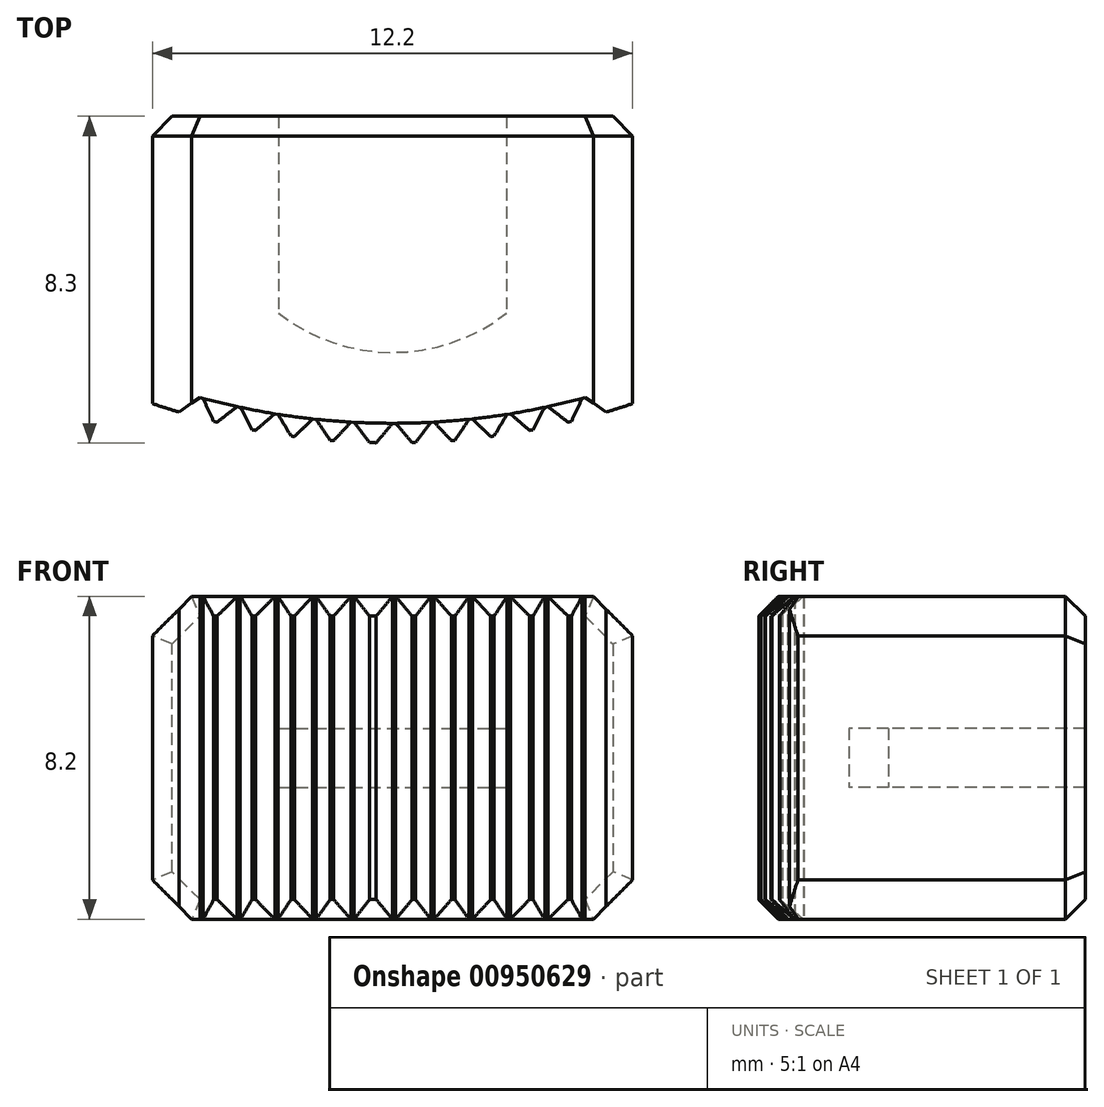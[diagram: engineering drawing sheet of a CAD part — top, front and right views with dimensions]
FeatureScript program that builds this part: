
annotation { "Feature Type Name" : "Feature", "Feature Type Description" : "" }
export const myFeature = defineFeature(function(context is Context, id is Id, definition is map)
    precondition{}
    {
        {
            var Q0;
            Q0=qCreatedBy(makeId("Top.planeOp"),FACE);
            var sketch = newSketch(context, id + "F0", { "sketchPlane" : qUnion([Q0])});
            skLineSegment(sketch, "E0", {"start": v(-6.1, -3.15) * mm, "end": v(-6.1, 4.15) * mm});
            skLineSegment(sketch, "E1", {"start": v(6.1, -3.15) * mm, "end": v(6.1, 4.15) * mm});
            skLineSegment(sketch, "E2", {"start": v(-6.1, 4.15) * mm, "end": v(6.1, 4.15) * mm});
            skArc(sketch, "E3", {"start": v(-6.1, -3.15) * mm, "mid": v(-5.76, -3.26) * mm, "end": v(-5.43, -3.36) * mm});
            skLineSegment(sketch, "E4", {"start": v(2.91, -3.42) * mm, "end": v(2.58, -3.98) * mm});
            skLineSegment(sketch, "E5", {"start": v(1.94, -3.55) * mm, "end": v(1.58, -4.08) * mm});
            skLineSegment(sketch, "E6", {"start": v(0.97, -3.62) * mm, "end": v(0.58, -4.14) * mm});
            skLineSegment(sketch, "E7", {"start": v(0, -3.65) * mm, "end": v(-0.42, -4.15) * mm});
            skLineSegment(sketch, "E8", {"start": v(3.87, -3.24) * mm, "end": v(3.56, -3.81) * mm});
            skLineSegment(sketch, "E9", {"start": v(4.82, -3.02) * mm, "end": v(4.54, -3.6) * mm});
            skLineSegment(sketch, "E10", {"start": v(0.08, -3.65) * mm, "end": v(0.5, -4.14) * mm});
            skLineSegment(sketch, "E11", {"start": v(1.05, -3.62) * mm, "end": v(1.5, -4.1) * mm});
            skLineSegment(sketch, "E12", {"start": v(2.03, -3.54) * mm, "end": v(2.5, -3.99) * mm});
            skLineSegment(sketch, "E13", {"start": v(3, -3.4) * mm, "end": v(3.48, -3.83) * mm});
            skLineSegment(sketch, "E14", {"start": v(3.95, -3.23) * mm, "end": v(4.46, -3.62) * mm});
            skLineSegment(sketch, "E15", {"start": v(4.9, -3) * mm, "end": v(5.43, -3.36) * mm});
            skLineSegment(sketch, "E16", {"start": v(-4.9, -3) * mm, "end": v(-5.43, -3.36) * mm});
            skLineSegment(sketch, "E17", {"start": v(-3.95, -3.23) * mm, "end": v(-4.46, -3.62) * mm});
            skLineSegment(sketch, "E18", {"start": v(-3, -3.4) * mm, "end": v(-3.48, -3.83) * mm});
            skLineSegment(sketch, "E19", {"start": v(-2.03, -3.54) * mm, "end": v(-2.5, -3.99) * mm});
            skLineSegment(sketch, "E20", {"start": v(-1.05, -3.62) * mm, "end": v(-1.5, -4.1) * mm});
            skLineSegment(sketch, "E21", {"start": v(-4.82, -3.02) * mm, "end": v(-4.54, -3.6) * mm});
            skLineSegment(sketch, "E22", {"start": v(-3.87, -3.24) * mm, "end": v(-3.56, -3.81) * mm});
            skLineSegment(sketch, "E23", {"start": v(-0.97, -3.62) * mm, "end": v(-0.58, -4.14) * mm});
            skLineSegment(sketch, "E24", {"start": v(-1.94, -3.55) * mm, "end": v(-1.58, -4.08) * mm});
            skLineSegment(sketch, "E25", {"start": v(-2.91, -3.42) * mm, "end": v(-2.58, -3.98) * mm});
            skArc(sketch, "E26.trimOffspring", {"start": v(-4.54, -3.6) * mm, "mid": v(-4.5, -3.61) * mm, "end": v(-4.46, -3.62) * mm});
            skArc(sketch, "E27.trimOffspring", {"start": v(-3.56, -3.81) * mm, "mid": v(-3.52, -3.82) * mm, "end": v(-3.48, -3.83) * mm});
            skArc(sketch, "E28.trimOffspring", {"start": v(-2.58, -3.98) * mm, "mid": v(-2.54, -3.98) * mm, "end": v(-2.5, -3.99) * mm});
            skArc(sketch, "E29.trimOffspring", {"start": v(-1.58, -4.08) * mm, "mid": v(-1.54, -4.09) * mm, "end": v(-1.5, -4.1) * mm});
            skArc(sketch, "E30.trimOffspring", {"start": v(-0.58, -4.14) * mm, "mid": v(-0.5, -4.14) * mm, "end": v(-0.42, -4.15) * mm});
            skArc(sketch, "E31.trimOffspring", {"start": v(0.5, -4.14) * mm, "mid": v(0.54, -4.14) * mm, "end": v(0.58, -4.14) * mm});
            skArc(sketch, "E32.trimOffspring", {"start": v(1.5, -4.1) * mm, "mid": v(1.54, -4.09) * mm, "end": v(1.58, -4.08) * mm});
            skArc(sketch, "E33.trimOffspring", {"start": v(2.5, -3.99) * mm, "mid": v(2.54, -3.98) * mm, "end": v(2.58, -3.98) * mm});
            skArc(sketch, "E34.trimOffspring", {"start": v(3.48, -3.83) * mm, "mid": v(3.52, -3.82) * mm, "end": v(3.56, -3.81) * mm});
            skArc(sketch, "E35.trimOffspring", {"start": v(4.46, -3.62) * mm, "mid": v(4.5, -3.61) * mm, "end": v(4.54, -3.6) * mm});
            skArc(sketch, "E36.trimOffspring", {"start": v(5.43, -3.36) * mm, "mid": v(5.76, -3.26) * mm, "end": v(6.1, -3.15) * mm});
            skLineSegment(sketch, "E37", {"start": v(-4.9, -3) * mm, "end": v(-4.82, -3.02) * mm});
            skLineSegment(sketch, "E38", {"start": v(-3.95, -3.23) * mm, "end": v(-3.87, -3.24) * mm});
            skLineSegment(sketch, "E39", {"start": v(-3, -3.4) * mm, "end": v(-2.91, -3.42) * mm});
            skLineSegment(sketch, "E40", {"start": v(-2.03, -3.54) * mm, "end": v(-1.94, -3.55) * mm});
            skLineSegment(sketch, "E41", {"start": v(-1.05, -3.62) * mm, "end": v(-0.97, -3.62) * mm});
            skLineSegment(sketch, "E42", {"start": v(0, -3.65) * mm, "end": v(0.08, -3.65) * mm});
            skLineSegment(sketch, "E43", {"start": v(0.97, -3.62) * mm, "end": v(1.05, -3.62) * mm});
            skLineSegment(sketch, "E44", {"start": v(1.94, -3.55) * mm, "end": v(2.03, -3.54) * mm});
            skLineSegment(sketch, "E45", {"start": v(2.91, -3.42) * mm, "end": v(3, -3.4) * mm});
            skLineSegment(sketch, "E46", {"start": v(3.87, -3.24) * mm, "end": v(3.95, -3.23) * mm});
            skLineSegment(sketch, "E47", {"start": v(4.82, -3.02) * mm, "end": v(4.9, -3) * mm});
            skSolve(sketch);
        }
        {
            var Q0;
            Q0=makeQuery(id+"F0.imprint","IMPRINT",FACE,{"disambiguationData":[TD([[makeQuery(id+"F0.imprint","IMPRINT",EDGE,{"derivedFrom":sQuery(id+"F0.wireOp",EDGE,"E0")}),-1.0]])]});
            extrude(context, id + "F1", {"entities" : qUnion([Q0]), "endBound" : BoundingType.SYMMETRIC, "depth" : 8.2 * mm, "offsetDistance" : 25 * mm});
        }
        {
            var Q0;
            Q0=qCreatedBy(makeId("Top.planeOp"),FACE);
            var sketch = newSketch(context, id + "F2", { "sketchPlane" : qUnion([Q0])});
            skLineSegment(sketch, "E48", {"start": v(-2.9, 4.15) * mm, "end": v(-2.9, -0.85) * mm});
            skLineSegment(sketch, "E49", {"start": v(2.9, 4.15) * mm, "end": v(2.9, -0.85) * mm});
            skLineSegment(sketch, "E50", {"start": v(-2.9, 4.15) * mm, "end": v(2.9, 4.15) * mm});
            skArc(sketch, "E51", {"start": v(-2.9, -0.85) * mm, "mid": v(0, -1.85) * mm, "end": v(2.9, -0.85) * mm});
            skSolve(sketch);
        }
        {
            var Q0;
            Q0 = qSketchRegion(id + "F2", true);
            extrude(context, id + "F3", {"entities" : qUnion([Q0]), "operationType" : NewBodyOperationType.REMOVE, "endBound" : BoundingType.SYMMETRIC, "depth" : 1.5 * mm, "offsetDistance" : 25 * mm});
        }
        {
            var Q0;
            Q0=makeQuery(id+"F1.opExtrude","CAP_EDGE",EDGE,{"disambiguationData":[OSD([sQuery(id+"F0.wireOp",EDGE,"E1")])],"isStart":true});
            var Q1;
            Q1=makeQuery(id+"F1.opExtrude","CAP_EDGE",EDGE,{"disambiguationData":[OSD([sQuery(id+"F0.wireOp",EDGE,"E0")])],"isStart":true});
            var Q2;
            Q2=makeQuery(id+"F1.opExtrude","CAP_EDGE",EDGE,{"disambiguationData":[OSD([sQuery(id+"F0.wireOp",EDGE,"E0")])],"isStart":false});
            var Q3;
            Q3=makeQuery(id+"F1.opExtrude","CAP_EDGE",EDGE,{"disambiguationData":[OSD([sQuery(id+"F0.wireOp",EDGE,"E1")])],"isStart":false});
            chamfer(context, id + "F4", {"entities" : qUnion([Q0, Q1, Q2, Q3]), "width" : 1 * mm, "tangentPropagation" : true});
        }
        {
            var Q0;
            Q0=makeQuery(id+"F1.opExtrude","CAP_EDGE",EDGE,{"disambiguationData":[OSD([sQuery(id+"F0.wireOp",EDGE,"E2")])],"isStart":true});
            var Q1;
            Q1=makeQuery(id+"F4.opChamfer","BLEND_EDGE",EDGE,{"blendedFrom":[makeQuery(id+"F1.opExtrude","CAP_EDGE",EDGE,{"disambiguationData":[OSD([sQuery(id+"F0.wireOp",EDGE,"E0")])],"isStart":true}),makeQuery(id+"F1.opExtrude","SWEPT_FACE",FACE,{"disambiguationData":[OSD([sQuery(id+"F0.wireOp",EDGE,"E2")])]})],"blendedInto":[makeQuery(id+"F1.opExtrude","SWEPT_FACE",FACE,{"disambiguationData":[OSD([sQuery(id+"F0.wireOp",EDGE,"E2")])]})]});
            var Q2;
            Q2=makeQuery(id+"F1.opExtrude","SWEPT_EDGE",EDGE,{"disambiguationData":[OSD([sQuery(id+"F0.wireOp",EDGE,"E0"),sQuery(id+"F0.wireOp",EDGE,"E2")])]});
            var Q3;
            Q3=makeQuery(id+"F4.opChamfer","BLEND_EDGE",EDGE,{"blendedFrom":[makeQuery(id+"F1.opExtrude","CAP_EDGE",EDGE,{"disambiguationData":[OSD([sQuery(id+"F0.wireOp",EDGE,"E1")])],"isStart":true}),makeQuery(id+"F1.opExtrude","SWEPT_FACE",FACE,{"disambiguationData":[OSD([sQuery(id+"F0.wireOp",EDGE,"E2")])]})],"blendedInto":[makeQuery(id+"F1.opExtrude","SWEPT_FACE",FACE,{"disambiguationData":[OSD([sQuery(id+"F0.wireOp",EDGE,"E2")])]})]});
            var Q4;
            Q4=makeQuery(id+"F1.opExtrude","SWEPT_EDGE",EDGE,{"disambiguationData":[OSD([sQuery(id+"F0.wireOp",EDGE,"E1"),sQuery(id+"F0.wireOp",EDGE,"E2")])]});
            var Q5;
            Q5=makeQuery(id+"F4.opChamfer","BLEND_EDGE",EDGE,{"blendedFrom":[makeQuery(id+"F1.opExtrude","CAP_EDGE",EDGE,{"disambiguationData":[OSD([sQuery(id+"F0.wireOp",EDGE,"E1")])],"isStart":false}),makeQuery(id+"F1.opExtrude","SWEPT_FACE",FACE,{"disambiguationData":[OSD([sQuery(id+"F0.wireOp",EDGE,"E2")])]})],"blendedInto":[makeQuery(id+"F1.opExtrude","SWEPT_FACE",FACE,{"disambiguationData":[OSD([sQuery(id+"F0.wireOp",EDGE,"E2")])]})]});
            var Q6;
            Q6=makeQuery(id+"F1.opExtrude","CAP_EDGE",EDGE,{"disambiguationData":[OSD([sQuery(id+"F0.wireOp",EDGE,"E2")])],"isStart":false});
            var Q7;
            Q7=makeQuery(id+"F4.opChamfer","BLEND_EDGE",EDGE,{"blendedFrom":[makeQuery(id+"F1.opExtrude","CAP_EDGE",EDGE,{"disambiguationData":[OSD([sQuery(id+"F0.wireOp",EDGE,"E0")])],"isStart":false}),makeQuery(id+"F1.opExtrude","SWEPT_FACE",FACE,{"disambiguationData":[OSD([sQuery(id+"F0.wireOp",EDGE,"E2")])]})],"blendedInto":[makeQuery(id+"F1.opExtrude","SWEPT_FACE",FACE,{"disambiguationData":[OSD([sQuery(id+"F0.wireOp",EDGE,"E2")])]})]});
            chamfer(context, id + "F5", {"entities" : qUnion([Q0, Q1, Q2, Q3, Q4, Q5, Q6, Q7]), "width" : 0.5 * mm, "tangentPropagation" : true});
        }
        {
            var Q0;
            Q0=makeQuery(id+"F1.opExtrude","CAP_EDGE",EDGE,{"disambiguationData":[OSD([sQuery(id+"F0.wireOp",EDGE,"E28.trimOffspring")])],"isStart":true});
            var Q1;
            Q1=makeQuery(id+"F1.opExtrude","CAP_EDGE",EDGE,{"disambiguationData":[OSD([sQuery(id+"F0.wireOp",EDGE,"E27.trimOffspring")])],"isStart":true});
            var Q2;
            Q2=makeQuery(id+"F1.opExtrude","CAP_EDGE",EDGE,{"disambiguationData":[OSD([sQuery(id+"F0.wireOp",EDGE,"E26.trimOffspring")])],"isStart":true});
            var Q3;
            Q3=makeQuery(id+"F1.opExtrude","CAP_EDGE",EDGE,{"disambiguationData":[OSD([sQuery(id+"F0.wireOp",EDGE,"E29.trimOffspring")])],"isStart":true});
            var Q4;
            Q4=makeQuery(id+"F1.opExtrude","CAP_EDGE",EDGE,{"disambiguationData":[OSD([sQuery(id+"F0.wireOp",EDGE,"E30.trimOffspring")])],"isStart":true});
            var Q5;
            Q5=makeQuery(id+"F1.opExtrude","CAP_EDGE",EDGE,{"disambiguationData":[OSD([sQuery(id+"F0.wireOp",EDGE,"E31.trimOffspring")])],"isStart":true});
            var Q6;
            Q6=makeQuery(id+"F1.opExtrude","CAP_EDGE",EDGE,{"disambiguationData":[OSD([sQuery(id+"F0.wireOp",EDGE,"E32.trimOffspring")])],"isStart":true});
            var Q7;
            Q7=makeQuery(id+"F1.opExtrude","CAP_EDGE",EDGE,{"disambiguationData":[OSD([sQuery(id+"F0.wireOp",EDGE,"E33.trimOffspring")])],"isStart":true});
            var Q8;
            Q8=makeQuery(id+"F1.opExtrude","CAP_EDGE",EDGE,{"disambiguationData":[OSD([sQuery(id+"F0.wireOp",EDGE,"E34.trimOffspring")])],"isStart":true});
            var Q9;
            Q9=makeQuery(id+"F1.opExtrude","CAP_EDGE",EDGE,{"disambiguationData":[OSD([sQuery(id+"F0.wireOp",EDGE,"E35.trimOffspring")])],"isStart":true});
            var Q10;
            Q10=makeQuery(id+"F1.opExtrude","CAP_EDGE",EDGE,{"disambiguationData":[OSD([sQuery(id+"F0.wireOp",EDGE,"E26.trimOffspring")])],"isStart":false});
            var Q11;
            Q11=makeQuery(id+"F1.opExtrude","CAP_EDGE",EDGE,{"disambiguationData":[OSD([sQuery(id+"F0.wireOp",EDGE,"E27.trimOffspring")])],"isStart":false});
            var Q12;
            Q12=makeQuery(id+"F1.opExtrude","CAP_EDGE",EDGE,{"disambiguationData":[OSD([sQuery(id+"F0.wireOp",EDGE,"E28.trimOffspring")])],"isStart":false});
            var Q13;
            Q13=makeQuery(id+"F1.opExtrude","CAP_EDGE",EDGE,{"disambiguationData":[OSD([sQuery(id+"F0.wireOp",EDGE,"E29.trimOffspring")])],"isStart":false});
            var Q14;
            Q14=makeQuery(id+"F1.opExtrude","CAP_EDGE",EDGE,{"disambiguationData":[OSD([sQuery(id+"F0.wireOp",EDGE,"E30.trimOffspring")])],"isStart":false});
            var Q15;
            Q15=makeQuery(id+"F1.opExtrude","CAP_EDGE",EDGE,{"disambiguationData":[OSD([sQuery(id+"F0.wireOp",EDGE,"E31.trimOffspring")])],"isStart":false});
            var Q16;
            Q16=makeQuery(id+"F1.opExtrude","CAP_EDGE",EDGE,{"disambiguationData":[OSD([sQuery(id+"F0.wireOp",EDGE,"E32.trimOffspring")])],"isStart":false});
            var Q17;
            Q17=makeQuery(id+"F1.opExtrude","CAP_EDGE",EDGE,{"disambiguationData":[OSD([sQuery(id+"F0.wireOp",EDGE,"E33.trimOffspring")])],"isStart":false});
            var Q18;
            Q18=makeQuery(id+"F1.opExtrude","CAP_EDGE",EDGE,{"disambiguationData":[OSD([sQuery(id+"F0.wireOp",EDGE,"E34.trimOffspring")])],"isStart":false});
            var Q19;
            Q19=makeQuery(id+"F1.opExtrude","CAP_EDGE",EDGE,{"disambiguationData":[OSD([sQuery(id+"F0.wireOp",EDGE,"E35.trimOffspring")])],"isStart":false});
            chamfer(context, id + "F6", {"entities" : qUnion([Q0, Q1, Q2, Q3, Q4, Q5, Q6, Q7, Q8, Q9, Q10, Q11, Q12, Q13, Q14, Q15, Q16, Q17, Q18, Q19]), "width" : 0.5 * mm, "tangentPropagation" : true});
        }
    });
